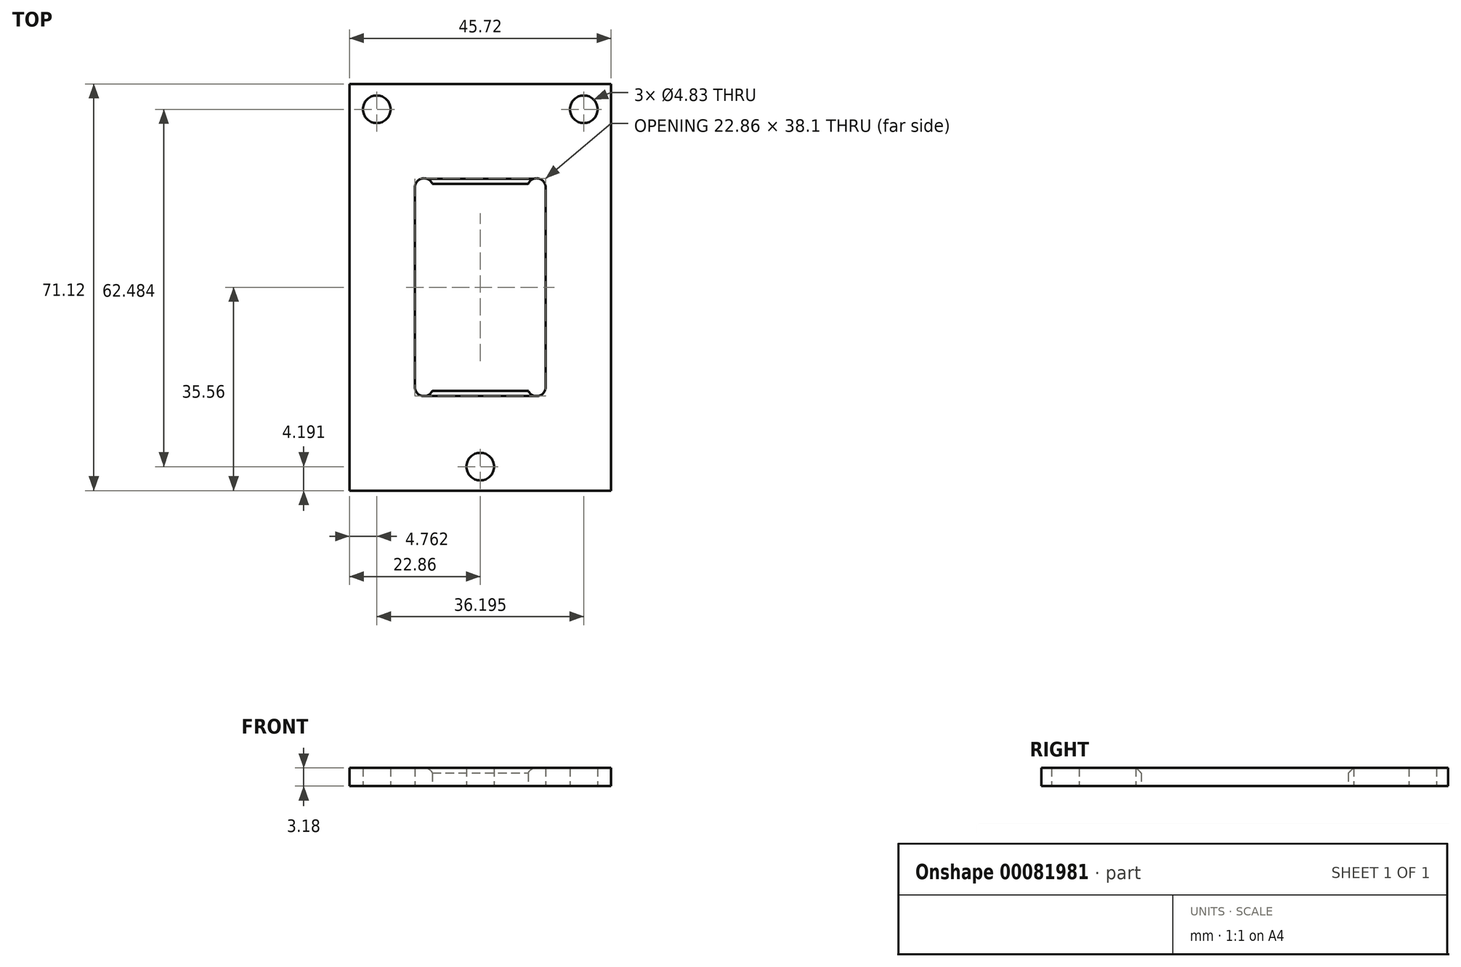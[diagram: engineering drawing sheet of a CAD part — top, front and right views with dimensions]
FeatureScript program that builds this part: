
annotation { "Feature Type Name" : "Feature", "Feature Type Description" : "" }
export const myFeature = defineFeature(function(context is Context, id is Id, definition is map)
    precondition{}
    {
        {
            var Q0;
            Q0=qCreatedBy(makeId("Top.planeOp"),FACE);
            var sketch = newSketch(context, id + "F0", { "sketchPlane" : qUnion([Q0])});
            skLineSegment(sketch, "E0.bottom", {"start": v(22.86, -35.56) * mm, "end": v(-22.86, -35.56) * mm});
            skLineSegment(sketch, "E0.top", {"start": v(22.86, 35.56) * mm, "end": v(-22.86, 35.56) * mm});
            skLineSegment(sketch, "E0.left", {"start": v(22.86, -35.56) * mm, "end": v(22.86, 35.56) * mm});
            skLineSegment(sketch, "E0.right", {"start": v(-22.86, -35.56) * mm, "end": v(-22.86, 35.56) * mm});
            skLineSegment(sketch, "E1.bottom", {"start": v(8.39, -18.1) * mm, "end": v(-8.39, -18.1) * mm});
            skLineSegment(sketch, "E1.top", {"start": v(8.39, 18.1) * mm, "end": v(-8.39, 18.1) * mm});
            skLineSegment(sketch, "E1.left", {"start": v(11.43, -17.46) * mm, "end": v(11.43, 17.46) * mm});
            skLineSegment(sketch, "E1.right", {"start": v(-11.43, -17.46) * mm, "end": v(-11.43, 17.46) * mm});
            skCircle(sketch, "E2", {"center": v(-18.1, 31.11) * mm, "radius": 2.41 * mm});
            skCircle(sketch, "E3.MirrorC", {"center": v(18.1, 31.11) * mm, "radius": 2.41 * mm});
            skPoint(sketch, "E4.endSnap0", {"position": v(0, -33.78) * mm});
            skCircle(sketch, "E5", {"center": v(0, -31.37) * mm, "radius": 2.41 * mm});
            skArc(sketch, "E6.MirrorC", {"start": v(-8.39, -18.1) * mm, "mid": v(-10.17, -19.02) * mm, "end": v(-11.43, -17.46) * mm});
            skArc(sketch, "E7.MirrorC", {"start": v(8.39, 18.1) * mm, "mid": v(10.17, 19.02) * mm, "end": v(11.43, 17.46) * mm});
            skArc(sketch, "E8.MirrorC", {"start": v(8.39, -18.1) * mm, "mid": v(10.17, -19.02) * mm, "end": v(11.43, -17.46) * mm});
            skArc(sketch, "E9.MirrorC", {"start": v(-8.39, 18.1) * mm, "mid": v(-10.17, 19.02) * mm, "end": v(-11.43, 17.46) * mm});
            skSolve(sketch);
        }
        {
            var Q0;
            Q0 = qSketchRegion(id + "F0", true);
            extrude(context, id + "F1", {"entities" : qUnion([Q0]), "depth" : 3.17 * mm});
        }
        {
            var Q0;
            Q0=makeQuery(id+"F1.opExtrude","CAP_EDGE",EDGE,{"disambiguationData":[OSD([sQuery(id+"F0.wireOp",EDGE,"E1.top")])],"isStart":false});
            var Q1;
            Q1=makeQuery(id+"F1.opExtrude","CAP_EDGE",EDGE,{"disambiguationData":[OSD([sQuery(id+"F0.wireOp",EDGE,"E1.bottom")])],"isStart":false});
            chamfer(context, id + "F2", {"entities" : qUnion([Q0, Q1]), "width" : 0.89 * mm, "tangentPropagation" : true});
        }
    });
